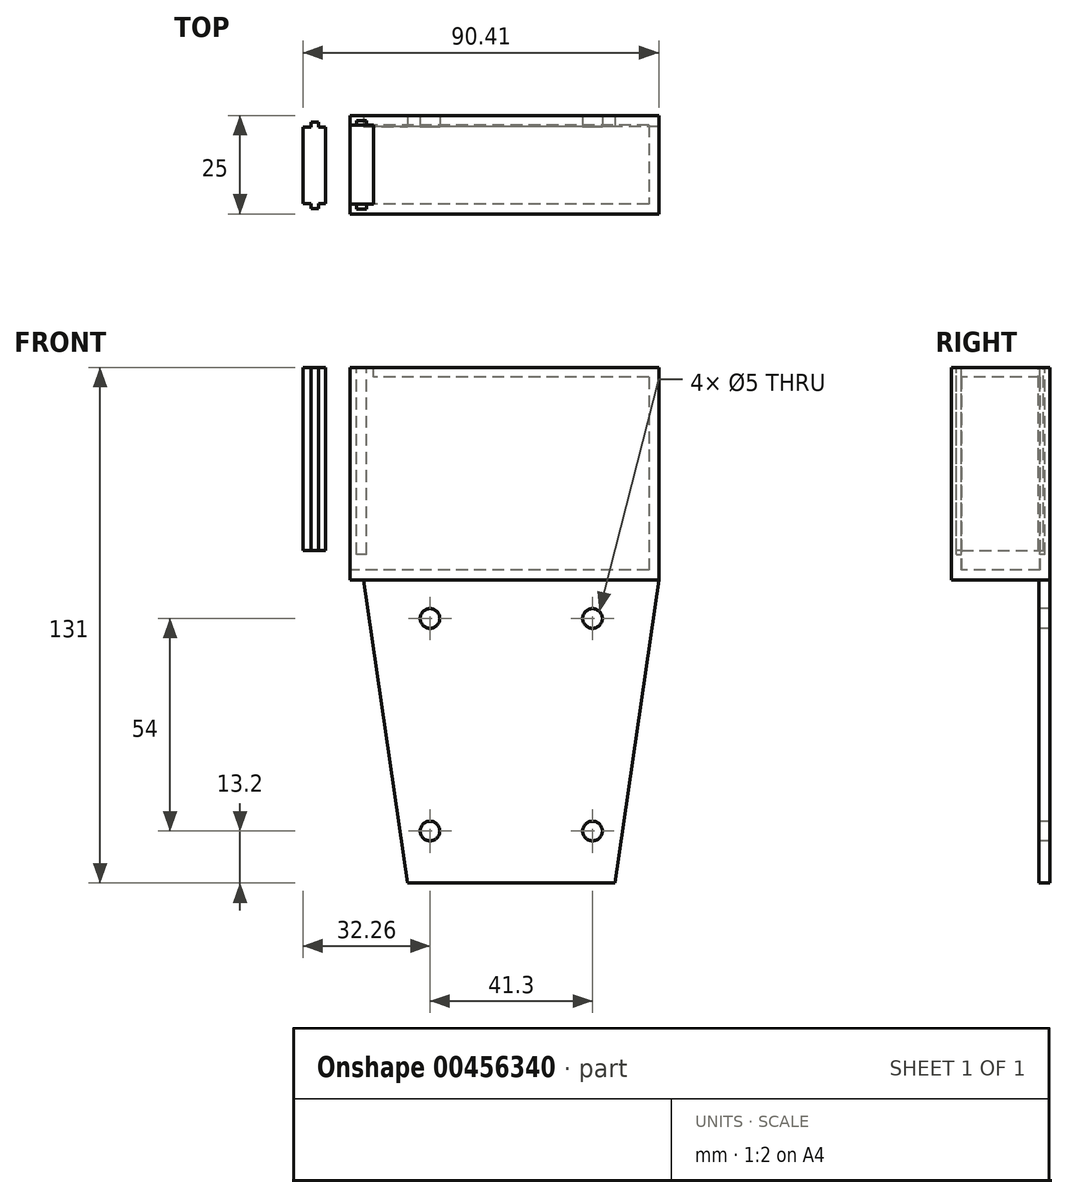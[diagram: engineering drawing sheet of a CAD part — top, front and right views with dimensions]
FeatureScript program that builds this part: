
annotation { "Feature Type Name" : "Feature", "Feature Type Description" : "" }
export const myFeature = defineFeature(function(context is Context, id is Id, definition is map)
    precondition{}
    {
        {
            var Q0;
            Q0=qCreatedBy(makeId("Front.planeOp"),FACE);
            var sketch = newSketch(context, id + "F0", { "sketchPlane" : qUnion([Q0])});
            skLineSegment(sketch, "E0.bottom", {"start": v(35, 24) * mm, "end": v(-35, 24) * mm});
            skLineSegment(sketch, "E0.top", {"start": v(35, -25) * mm, "end": v(-35, -25) * mm});
            skLineSegment(sketch, "E0.left", {"start": v(35, 24) * mm, "end": v(35, -25) * mm});
            skLineSegment(sketch, "E0.right", {"start": v(-35, 24) * mm, "end": v(-35, -25) * mm});
            skPoint(sketch, "E0.middle", {"position": v(0, -0.5) * mm});
            skLineSegment(sketch, "E1.0", {"start": v(37.5, 26.5) * mm, "end": v(-37.5, 26.5) * mm});
            skLineSegment(sketch, "E1.1", {"start": v(37.5, 26.5) * mm, "end": v(37.5, -27.5) * mm});
            skLineSegment(sketch, "E1.3", {"start": v(-37.5, 26.5) * mm, "end": v(-37.5, -27.5) * mm});
            skLineSegment(sketch, "E2", {"start": v(-35, 24) * mm, "end": v(-35, 26.5) * mm});
            skLineSegment(sketch, "E3", {"start": v(-35, -25) * mm, "end": v(-35, -27.5) * mm});
            skLineSegment(sketch, "E4", {"start": v(-37.5, -27.5) * mm, "end": v(-41, -27.5) * mm});
            skLineSegment(sketch, "E5", {"start": v(-41, -27.5) * mm, "end": v(-41, -25) * mm});
            skLineSegment(sketch, "E6", {"start": v(-41, -25) * mm, "end": v(-37.5, -25) * mm});
            skLineSegment(sketch, "E7", {"start": v(-37.5, -25) * mm, "end": v(-35, -25) * mm});
            skLineSegment(sketch, "E8.bottom", {"start": v(26.35, -104.5) * mm, "end": v(26.35, -28.3) * mm});
            skLineSegment(sketch, "E8.top", {"start": v(-26.35, -104.5) * mm, "end": v(-26.35, -28.3) * mm});
            skLineSegment(sketch, "E8.left", {"start": v(26.35, -104.5) * mm, "end": v(-26.35, -104.5) * mm});
            skLineSegment(sketch, "E8.right", {"start": v(26.35, -28.3) * mm, "end": v(-26.35, -28.3) * mm});
            skPoint(sketch, "E8.middle", {"position": v(0, -66.4) * mm});
            skLineSegment(sketch, "E9", {"start": v(26.35, -37.3) * mm, "end": v(20.65, -37.3) * mm, "construction": true});
            skLineSegment(sketch, "E10", {"start": v(-20.65, -37.3) * mm, "end": v(-26.35, -37.3) * mm, "construction": true});
            skLineSegment(sketch, "E11", {"start": v(20.65, -104.5) * mm, "end": v(20.65, -91.3) * mm, "construction": true});
            skLineSegment(sketch, "E12", {"start": v(-20.65, -91.3) * mm, "end": v(-20.65, -104.5) * mm, "construction": true});
            skLineSegment(sketch, "E13", {"start": v(20.65, -91.3) * mm, "end": v(26.35, -91.3) * mm, "construction": true});
            skLineSegment(sketch, "E14", {"start": v(-20.65, -91.3) * mm, "end": v(-26.35, -91.3) * mm, "construction": true});
            skLineSegment(sketch, "E15", {"start": v(-20.65, -37.3) * mm, "end": v(-20.65, -28.3) * mm, "construction": true});
            skLineSegment(sketch, "E16", {"start": v(20.65, -37.3) * mm, "end": v(20.65, -28.3) * mm, "construction": true});
            skCircle(sketch, "E17", {"center": v(20.65, -37.3) * mm, "radius": 2.5 * mm});
            skCircle(sketch, "E18", {"center": v(20.65, -91.3) * mm, "radius": 2.5 * mm});
            skCircle(sketch, "E19.MirrorC", {"center": v(-20.65, -37.3) * mm, "radius": 2.5 * mm});
            skCircle(sketch, "E20.MirrorC", {"center": v(-20.65, -91.3) * mm, "radius": 2.5 * mm});
            skLineSegment(sketch, "E21.2", {"start": v(37.5, -27.5) * mm, "end": v(-37.5, -27.5) * mm});
            skLineSegment(sketch, "E22", {"start": v(-26.35, -28.3) * mm, "end": v(-26.35, -27.5) * mm});
            skLineSegment(sketch, "E23", {"start": v(26.35, -27.5) * mm, "end": v(26.35, -28.3) * mm});
            skLineSegment(sketch, "E24", {"start": v(37.5, -27.5) * mm, "end": v(26.35, -104.5) * mm});
            skLineSegment(sketch, "E25", {"start": v(-37.5, -27.5) * mm, "end": v(-26.35, -104.5) * mm});
            skLineSegment(sketch, "E26", {"start": v(0, -66.4) * mm, "end": v(0, -27.5) * mm});
            skLineSegment(sketch, "E27", {"start": v(-35, -27.5) * mm, "end": v(0, -27.5) * mm});
            skSolve(sketch);
        }
        {
            var Q0;
            Q0=makeQuery(id+"F0.imprint","IMPRINT",FACE,{"disambiguationData":[TD([[makeQuery(id+"F0.imprint","IMPRINT",EDGE,{"derivedFrom":sQuery(id+"F0.wireOp",EDGE,"E0.bottom")}),-1.0]])]});
            var Q1;
            Q1=makeQuery(id+"F0.imprint","IMPRINT",FACE,{"disambiguationData":[TD([[makeQuery(id+"F0.imprint","IMPRINT",EDGE,{"derivedFrom":sQuery(id+"F0.wireOp",EDGE,"E0.bottom")}),1.0]])]});
            var Q2;
            Q2=makeQuery(id+"F0.imprint","IMPRINT",FACE,{"disambiguationData":[TD([[makeQuery(id+"F0.imprint","IMPRINT",EDGE,{"derivedFrom":sQuery(id+"F0.wireOp",EDGE,"471ba2c4-f0ab-47da-b2d1-09421f94a4d20.MirrorCS")}),-1.0]])]});
            var Q3;
            Q3=makeQuery(id+"F0.imprint","IMPRINT",FACE,{"disambiguationData":[TD([[makeQuery(id+"F0.imprint","IMPRINT",EDGE,{"derivedFrom":sQuery(id+"F0.wireOp",EDGE,"E8.bottom")}),-1.0]])]});
            var Q4;
            {var subQ0=sQuery(id+"F0.wireOp",EDGE,"E22");Q4=makeQuery(id+"F0.imprint","IMPRINT",FACE,{"disambiguationData":[TD([[makeQuery(id+"F0.imprint","IMPRINT",EDGE,{"derivedFrom":subQ0}),-1.0]])]});}
            var Q5;
            {var subQ0=sQuery(id+"F0.wireOp",EDGE,"E23");Q5=makeQuery(id+"F0.imprint","IMPRINT",FACE,{"disambiguationData":[TD([[makeQuery(id+"F0.imprint","IMPRINT",EDGE,{"derivedFrom":subQ0}),-1.0]])]});}
            var Q6;
            {var subQ1=sQuery(id+"F0.wireOp",EDGE,"E8.bottom");Q6=makeQuery(id+"F0.imprint","IMPRINT",FACE,{"disambiguationData":[TD([[makeQuery(id+"F0.imprint","IMPRINT",EDGE,{"derivedFrom":subQ1}),1.0]])]});}
            var Q7;
            Q7=makeQuery(id+"F0.imprint","IMPRINT",FACE,{"disambiguationData":[TD([[makeQuery(id+"F0.imprint","IMPRINT",EDGE,{"derivedFrom":sQuery(id+"F0.wireOp",EDGE,"E8.top")}),1.0]])]});
            var Q8;
            Q8=makeQuery(id+"F0.imprint","IMPRINT",FACE,{"disambiguationData":[TD([[makeQuery(id+"F0.imprint","IMPRINT",EDGE,{"derivedFrom":sQuery(id+"F0.wireOp",EDGE,"E5")}),-1.0]])]});
            var Q9;
            {var subQ4=sQuery(id+"F0.wireOp",EDGE,"E3");Q9=makeQuery(id+"F0.imprint","IMPRINT",FACE,{"disambiguationData":[TD([[makeQuery(id+"F0.imprint","IMPRINT",EDGE,{"derivedFrom":subQ4}),-1.0]])]});}
            extrude(context, id + "F1", {"entities" : qUnion([Q0, Q1, Q2, Q3, Q4, Q5, Q6, Q7, Q8, Q9]), "oppositeDirection" : true, "depth" : 25 * mm});
        }
        {
            var Q0;
            Q0=makeQuery(id+"F0.imprint","IMPRINT",FACE,{"disambiguationData":[TD([[makeQuery(id+"F0.imprint","IMPRINT",EDGE,{"derivedFrom":sQuery(id+"F0.wireOp",EDGE,"471ba2c4-f0ab-47da-b2d1-09421f94a4d20.MirrorCS")}),-1.0]])]});
            var Q1;
            Q1=makeQuery(id+"F0.imprint","IMPRINT",FACE,{"disambiguationData":[TD([[makeQuery(id+"F0.imprint","IMPRINT",EDGE,{"derivedFrom":sQuery(id+"F0.wireOp",EDGE,"E0.bottom")}),1.0]])]});
            extrude(context, id + "F2", {"entities" : qUnion([Q0, Q1]), "operationType" : NewBodyOperationType.REMOVE, "oppositeDirection" : true, "depth" : 22.5 * mm});
        }
        {
            var Q0;
            Q0=makeQuery(id+"F0.imprint","IMPRINT",FACE,{"disambiguationData":[TD([[makeQuery(id+"F0.imprint","IMPRINT",EDGE,{"derivedFrom":sQuery(id+"F0.wireOp",EDGE,"E0.bottom")}),1.0]])]});
            extrude(context, id + "F3", {"entities" : qUnion([Q0]), "operationType" : NewBodyOperationType.ADD, "oppositeDirection" : true, "depth" : 2.5 * mm});
        }
        {
            var Q0;
            Q0=makeQuery(id+"F1.opExtrude","CAP_EDGE",EDGE,{"disambiguationData":[OSD([sQuery(id+"F0.wireOp",EDGE,"E1.0")])],"isStart":true});
            cPoint(context, id + "F4", {"entities" : qUnion([Q0]), "parameter" : 0.5});
        }
        {
            var Q0;
            Q0=makeQuery(id+"F1.opExtrude","CAP_VERTEX",VERTEX,{"disambiguationData":[OSD([sQuery(id+"F0.wireOp",EDGE,"E1.0"),sQuery(id+"F0.wireOp",EDGE,"E2")])],"isStart":false});
            var Q1;
            Q1=makeQuery(id+"F1.opExtrude","CAP_VERTEX",VERTEX,{"disambiguationData":[OSD([sQuery(id+"F0.wireOp",EDGE,"E1.0"),sQuery(id+"F0.wireOp",EDGE,"E2")])],"isStart":true});
            var Q2;
            Q2 = qCreatedBy(id + "F4" ,VERTEX);
            cPlane(context, id + "F5", {"entities" : qUnion([Q0, Q1, Q2]), "cplaneType" : CPlaneType.THREE_POINT, "offset" : 25 * mm, "width" : 150 * mm, "height" : 150 * mm});
        }
        {
            var Q0;
            Q0=qCreatedBy(id+"F5.planeOp",FACE);
            var sketch = newSketch(context, id + "F6", { "sketchPlane" : qUnion([Q0])});
            skLineSegment(sketch, "E28", {"start": v(0, 0) * mm, "end": v(-35, 0) * mm});
            skLineSegment(sketch, "E29", {"start": v(-35, 0) * mm, "end": v(-35, -25) * mm});
            skLineSegment(sketch, "E30", {"start": v(-35, -25) * mm, "end": v(0, -25) * mm});
            skLineSegment(sketch, "E31", {"start": v(-35, 0) * mm, "end": v(-41, 0) * mm});
            skLineSegment(sketch, "E32", {"start": v(-41, 0) * mm, "end": v(-41, -2.5) * mm});
            skLineSegment(sketch, "E33", {"start": v(-41, -2.5) * mm, "end": v(-39.25, -2.5) * mm});
            skLineSegment(sketch, "E34", {"start": v(-39.25, -2.5) * mm, "end": v(-39.25, -1.25) * mm});
            skLineSegment(sketch, "E35", {"start": v(-39.25, -1.25) * mm, "end": v(-36.75, -1.25) * mm});
            skLineSegment(sketch, "E36", {"start": v(-36.75, -1.25) * mm, "end": v(-36.75, -2.5) * mm});
            skLineSegment(sketch, "E37", {"start": v(-36.75, -2.5) * mm, "end": v(-35, -2.5) * mm});
            skPoint(sketch, "E38.endSnap0", {"position": v(-35, -12.5) * mm});
            skLineSegment(sketch, "E39", {"start": v(-36.75, -2.5) * mm, "end": v(-39.25, -2.5) * mm});
            skLineSegment(sketch, "E40.MirrorCS", {"start": v(-39.25, -22.5) * mm, "end": v(-39.25, -23.75) * mm});
            skLineSegment(sketch, "E41.MirrorCS", {"start": v(-41, -22.5) * mm, "end": v(-39.25, -22.5) * mm});
            skLineSegment(sketch, "E42.MirrorCS", {"start": v(-36.75, -23.75) * mm, "end": v(-36.75, -22.5) * mm});
            skLineSegment(sketch, "E43.MirrorCS", {"start": v(-36.75, -22.5) * mm, "end": v(-39.25, -22.5) * mm});
            skLineSegment(sketch, "E44.MirrorCS", {"start": v(-36.75, -22.5) * mm, "end": v(-35, -22.5) * mm});
            skLineSegment(sketch, "E45.MirrorCS", {"start": v(-35, -25) * mm, "end": v(-41, -25) * mm});
            skLineSegment(sketch, "E46.MirrorCS", {"start": v(-39.25, -23.75) * mm, "end": v(-36.75, -23.75) * mm});
            skLineSegment(sketch, "E47.MirrorCS", {"start": v(-41, -25) * mm, "end": v(-41, -22.5) * mm});
            skPoint(sketch, "E48.endSnap0", {"position": v(-46.91, -12.3) * mm});
            skPoint(sketch, "E49.endSnap0", {"position": v(-52.04, -22.3) * mm});
            skLineSegment(sketch, "E50", {"start": v(-52.91, -22.06) * mm, "end": v(-50.91, -22.06) * mm});
            skLineSegment(sketch, "E51", {"start": v(-50.91, -22.06) * mm, "end": v(-50.91, -23.3) * mm});
            skLineSegment(sketch, "E52", {"start": v(-50.91, -23.3) * mm, "end": v(-48.91, -23.3) * mm});
            skLineSegment(sketch, "E53", {"start": v(-48.91, -23.3) * mm, "end": v(-48.91, -22.06) * mm});
            skLineSegment(sketch, "E54", {"start": v(-48.91, -22.06) * mm, "end": v(-47.16, -22.06) * mm});
            skLineSegment(sketch, "E55.MirrorCS", {"start": v(-48.91, -1.3) * mm, "end": v(-48.91, -2.56) * mm});
            skLineSegment(sketch, "E56.MirrorCS", {"start": v(-50.91, -2.56) * mm, "end": v(-50.91, -1.3) * mm});
            skLineSegment(sketch, "E57.MirrorCS", {"start": v(-50.91, -1.3) * mm, "end": v(-48.91, -1.3) * mm});
            skLineSegment(sketch, "E58.MirrorCS", {"start": v(-52.91, -2.56) * mm, "end": v(-50.91, -2.56) * mm});
            skLineSegment(sketch, "E59.MirrorCS", {"start": v(-48.91, -2.56) * mm, "end": v(-47.16, -2.56) * mm});
            skPoint(sketch, "E60.MirrorP", {"position": v(-52.04, -2.3) * mm});
            skLineSegment(sketch, "E61", {"start": v(-52.91, -2.56) * mm, "end": v(-52.91, -22.06) * mm});
            skLineSegment(sketch, "E62", {"start": v(-47.16, -22.06) * mm, "end": v(-47.16, -2.56) * mm});
            skSolve(sketch);
        }
        {
            var Q0;
            Q0=makeQuery(id+"F6.imprint","IMPRINT",FACE,{"disambiguationData":[TD([[makeQuery(id+"F6.imprint","IMPRINT",EDGE,{"derivedFrom":sQuery(id+"F6.wireOp",EDGE,"E40.MirrorCS")}),-1.0]])]});
            var Q1;
            {var subQ0=sQuery(id+"F6.wireOp",EDGE,"E31");Q1=makeQuery(id+"F6.imprint","IMPRINT",FACE,{"disambiguationData":[TD([[makeQuery(id+"F6.imprint","IMPRINT",EDGE,{"derivedFrom":subQ0}),1.0]])]});}
            var Q2;
            Q2=makeQuery(id+"F6.imprint","IMPRINT",FACE,{"disambiguationData":[TD([[makeQuery(id+"F6.imprint","IMPRINT",EDGE,{"derivedFrom":sQuery(id+"F6.wireOp",EDGE,"E34")}),-1.0]])]});
            var Q3;
            Q3=makeQuery(id+"F6.imprint","IMPRINT",FACE,{"disambiguationData":[TD([[makeQuery(id+"F6.imprint","IMPRINT",EDGE,{"derivedFrom":sQuery(id+"F6.wireOp",EDGE,"E40.MirrorCS")}),1.0]])]});
            extrude(context, id + "F7", {"entities" : qUnion([Q0, Q1, Q2, Q3]), "operationType" : NewBodyOperationType.ADD, "depth" : 51.5 * mm});
        }
        {
            var Q0;
            Q0=makeQuery(id+"F6.imprint","IMPRINT",FACE,{"disambiguationData":[TD([[makeQuery(id+"F6.imprint","IMPRINT",EDGE,{"derivedFrom":sQuery(id+"F6.wireOp",EDGE,"E40.MirrorCS")}),1.0]])]});
            var Q1;
            Q1=makeQuery(id+"F6.imprint","IMPRINT",FACE,{"disambiguationData":[TD([[makeQuery(id+"F6.imprint","IMPRINT",EDGE,{"derivedFrom":sQuery(id+"F6.wireOp",EDGE,"E34")}),-1.0]])]});
            extrude(context, id + "F8", {"entities" : qUnion([Q0, Q1]), "operationType" : NewBodyOperationType.REMOVE, "depth" : 47.5 * mm});
        }
        {
            var Q0;
            Q0=makeQuery(id+"F6.imprint","IMPRINT",FACE,{"disambiguationData":[TD([[makeQuery(id+"F6.imprint","IMPRINT",EDGE,{"derivedFrom":sQuery(id+"F6.wireOp",EDGE,"E50")}),1.0]])]});
            extrude(context, id + "F9", {"entities" : qUnion([Q0]), "depth" : 46.5 * mm});
        }
        {
            var Q0;
            Q0=makeQuery(id+"F0.imprint","IMPRINT",FACE,{"disambiguationData":[TD([[makeQuery(id+"F0.imprint","IMPRINT",EDGE,{"derivedFrom":sQuery(id+"F0.wireOp",EDGE,"E8.top")}),1.0]])]});
            var Q1;
            {var subQ1=sQuery(id+"F0.wireOp",EDGE,"E8.bottom");Q1=makeQuery(id+"F0.imprint","IMPRINT",FACE,{"disambiguationData":[TD([[makeQuery(id+"F0.imprint","IMPRINT",EDGE,{"derivedFrom":subQ1}),1.0]])]});}
            var Q2;
            Q2=makeQuery(id+"F0.imprint","IMPRINT",FACE,{"disambiguationData":[TD([[makeQuery(id+"F0.imprint","IMPRINT",EDGE,{"derivedFrom":sQuery(id+"F0.wireOp",EDGE,"E8.bottom")}),-1.0]])]});
            var Q3;
            {var subQ0=sQuery(id+"F0.wireOp",EDGE,"E22");Q3=makeQuery(id+"F0.imprint","IMPRINT",FACE,{"disambiguationData":[TD([[makeQuery(id+"F0.imprint","IMPRINT",EDGE,{"derivedFrom":subQ0}),-1.0]])]});}
            var Q4;
            {var subQ0=sQuery(id+"F0.wireOp",EDGE,"E23");Q4=makeQuery(id+"F0.imprint","IMPRINT",FACE,{"disambiguationData":[TD([[makeQuery(id+"F0.imprint","IMPRINT",EDGE,{"derivedFrom":subQ0}),-1.0]])]});}
            extrude(context, id + "F10", {"entities" : qUnion([Q0, Q1, Q2, Q3, Q4]), "operationType" : NewBodyOperationType.REMOVE, "oppositeDirection" : true, "depth" : 22.2 * mm});
        }
    });
